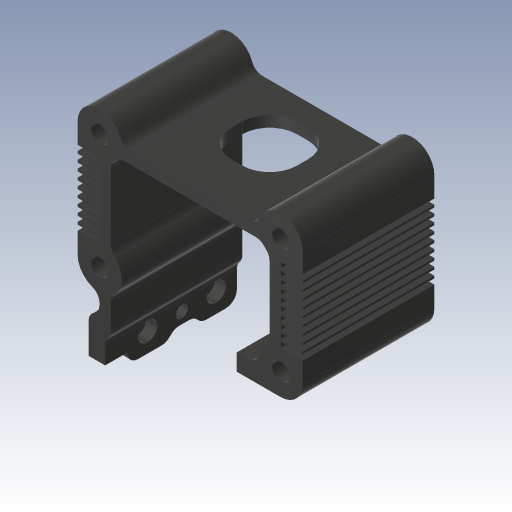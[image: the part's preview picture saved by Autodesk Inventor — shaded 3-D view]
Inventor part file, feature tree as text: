
AUTODESK INVENTOR PART (.ipt)
format: ipt  version: 2023.3 (Build 273359000, 359)  size: 701,952 bytes
history: native  units: in
note: dims shown in document units (in); Inventor stores cm internally (conversion verified against a paired STEP export)
features: sketch x6, extrude x6, fillet x5, hole x5, projected_geometry x3, pattern_linear x1
ambient origin geometry x8: Origin, YZ Plane, XZ Plane, XY Plane, X Axis, Y Axis, Z Axis, Center Point
bodies: Body1 (feature_tree)
feature tree (26):
  sketch  "Skizze3"  dims[d4=0.2559in d6=0.1181in d7=0.0787in d8=0.0787in]
  extrude  "Extrusion3"  Depth=0.1181in
  fillet  "Rundung1"  Radius=0.0787in
  hole  "Bohrung1"  [1 undecoded]
  extrude  "Extrusion4"  Depth=0.3543in
  pattern_linear  "Rechteckige Anordnung1"  Count1=2 Spacing1=0.0in
  sketch  "Skizze7"  dims[d15=1.1417in d17=0.3543in d20=0.7874in d21=0.0in]
  extrude  "Extrusion11"  Depth=0.0787in
  fillet  "Rundung2"  Radius=0.315in
  extrude  "Extrusion8"  Depth=0.315in
  fillet  "Rundung3"  Radius=0.315in
  extrude  "Extrusion9"  Depth=0.1575in
  sketch  "Skizze12"  dims[d31=0.748in d32=0.126in d33=0.1575in d34=0.2559in d35=0.1339in d36=90.0deg d37=0.1969in d38=0.0in d39=0.1575in d40=0.0394in d41=0.1575in d42=0.0394in d43=0.0in d44=0.0in d45=3.937in d47=0.0551in d55=0.0787in d57=0.2953in d58=0.2953in d67=0.1476in d68=0.1476in d83=0.0787in d84=0.4724in d85=0.4724in d88=0.3937in d89=0.0in d90=0.1969in d95=0.1575in d96=0.0in d98=0.1181in d99=1.2598in d100=0.315in d101=0.748in d104=0.0787in d107=0.2953in d112=0.1378in d113=0.2362in d114=0.4331in d115=0.0787in d116=90.0deg d117=0.0787in d118=0.0in d119=0.0787in d120=0.1378in d122=0.0866in d123=0.1969in d124=0.1732in d125=0.0787in d126=90.0deg d127=0.2756in d128=0.0in d129=0.0787in d130=0.0in d131=0.0in d132=0.1969in d133=0.0591in d134=0.1476in d135=0.1476in d136=0.1378in d137=0.2362in d138=0.1575in d139=0.0787in d140=90.0deg d141=0.0787in d142=0.0in d143=0.0617in d144=0.248in d145=0.1575in d146=0.0787in d147=90.0deg d148=0.248in d149=0.0in d150=0.1969in d151=0.0in d152=0.0787in d153=0.0197in d154=0.8268in d155=0.0315in]
  hole  "Bohrung4"  [1 undecoded]
  fillet  "Rundung6"  Radius=0.1575in
  hole  "Bohrung5"  [1 undecoded]
  hole  "Bohrung6"  [1 undecoded]
  hole  "Bohrung7"  [1 undecoded]
  extrude  "Extrusion12"  Depth=0.0787in
  fillet  "Rundung7"  Radius=0.2953in
  sketch  "Skizze4"  dims[d10=0.0787in d12=0.1181in]
  sketch  "Skizze9"  dims[d22=1.1417in d25=0.0787in d26=0.315in]
  sketch  "Skizze11"  dims[d27=0.315in d28=0.315in d29=0.315in]
  projected_geometry  "Projizierte Kontur4"
  projected_geometry  "Projizierte Kontur6"
  projected_geometry  "Projizierte Kontur7"
note: 5 required parameter values undecoded (feature->parameter linkage not recoverable at this tier; creation-order binding heuristic only, values carry confidence <= 0.55)
